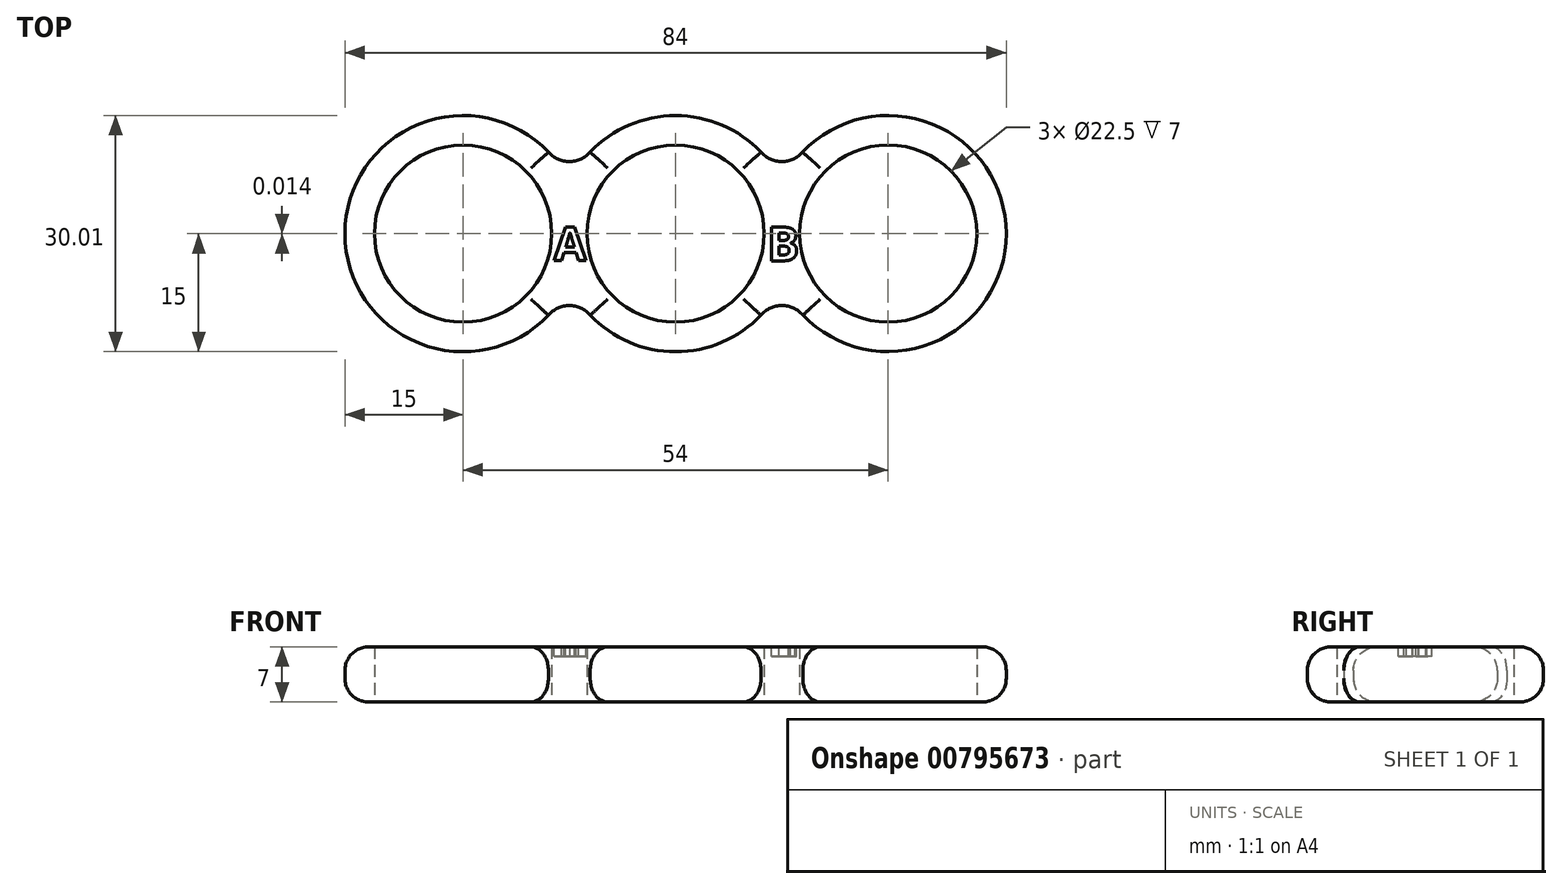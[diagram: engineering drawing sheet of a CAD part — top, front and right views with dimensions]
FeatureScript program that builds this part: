
annotation { "Feature Type Name" : "Feature", "Feature Type Description" : "" }
export const myFeature = defineFeature(function(context is Context, id is Id, definition is map)
    precondition{}
    {
        {
            var Q0;
            Q0=qCreatedBy(makeId("Top.planeOp"),FACE);
            var sketch = newSketch(context, id + "F0", { "sketchPlane" : qUnion([Q0])});
            skCircle(sketch, "E0", {"center": v(0, 0) * mm, "radius": 11.25 * mm});
            skCircle(sketch, "E1", {"center": v(0, 0) * mm, "radius": 4 * mm});
            skCircle(sketch, "E2", {"center": v(27, 0.01) * mm, "radius": 11.25 * mm});
            skCircle(sketch, "E3", {"center": v(27, 0.01) * mm, "radius": 4 * mm});
            skCircle(sketch, "E4", {"center": v(-27, 0) * mm, "radius": 4 * mm});
            skCircle(sketch, "E5", {"center": v(-27, 0) * mm, "radius": 11.25 * mm});
            skPoint(sketch, "E6.first.point", {"position": v(-16.16, 10.36) * mm});
            skPoint(sketch, "E6.second.point", {"position": v(-10.84, 10.36) * mm});
            skPoint(sketch, "E7.first.point", {"position": v(10.84, 10.36) * mm});
            skPoint(sketch, "E7.second.point", {"position": v(16.14, 10.36) * mm});
            skLineSegment(sketch, "E8", {"start": v(-16.16, 10.36) * mm, "end": v(-16.16, 10.36) * mm});
            skArc(sketch, "E9", {"start": v(10.84, 10.36) * mm, "mid": v(13.5, 9.15) * mm, "end": v(16.14, 10.36) * mm});
            skLineSegment(sketch, "E10", {"start": v(16.14, 10.36) * mm, "end": v(16.14, 10.36) * mm});
            skArc(sketch, "E11", {"start": v(10.84, 10.36) * mm, "mid": v(0, 15) * mm, "end": v(-10.84, 10.36) * mm});
            skPoint(sketch, "E12.first.point", {"position": v(-16.15, -10.36) * mm});
            skPoint(sketch, "E12.second.point", {"position": v(-10.85, -10.36) * mm});
            skPoint(sketch, "E12.third.point", {"position": v(-13.67, -16.14) * mm});
            skPoint(sketch, "E13.first.point", {"position": v(10.85, -10.35) * mm});
            skPoint(sketch, "E13.second.point", {"position": v(16.16, -10.35) * mm});
            skPoint(sketch, "E13.third.point", {"position": v(14.19, -16.07) * mm});
            skLineSegment(sketch, "E14", {"start": v(-10.85, -10.36) * mm, "end": v(-10.85, -10.36) * mm});
            skArc(sketch, "E15", {"start": v(-10.85, -10.36) * mm, "mid": v(-13.5, -9.14) * mm, "end": v(-16.15, -10.36) * mm});
            skLineSegment(sketch, "E16", {"start": v(-16.15, -10.36) * mm, "end": v(-16.15, -10.36) * mm});
            skArc(sketch, "E17", {"start": v(-13.5, -6.54) * mm, "mid": v(-13.5, -6.55) * mm, "end": v(-13.49, -6.57) * mm});
            skArc(sketch, "E18", {"start": v(-16.16, 10.36) * mm, "mid": v(-13.5, 9.14) * mm, "end": v(-10.84, 10.36) * mm});
            skArc(sketch, "E19", {"start": v(-16.16, 10.36) * mm, "mid": v(-42, 0) * mm, "end": v(-16.15, -10.36) * mm});
            skArc(sketch, "E20", {"start": v(-10.85, -10.36) * mm, "mid": v(0, -15) * mm, "end": v(10.85, -10.35) * mm});
            skLineSegment(sketch, "E21", {"start": v(-13.49, -6.57) * mm, "end": v(-13.49, -6.57) * mm});
            skArc(sketch, "E22", {"start": v(16.16, -10.35) * mm, "mid": v(42, 0.03) * mm, "end": v(16.14, 10.36) * mm});
            skLineSegment(sketch, "E23", {"start": v(13.5, 6.55) * mm, "end": v(13.5, 6.55) * mm});
            skArc(sketch, "E24", {"start": v(16.16, -10.35) * mm, "mid": v(13.5, -9.14) * mm, "end": v(10.85, -10.35) * mm});
            skLineSegment(sketch, "E25", {"start": v(10.85, -10.35) * mm, "end": v(10.85, -10.35) * mm});
            skArc(sketch, "E26", {"start": v(13.51, 6.51) * mm, "mid": v(13.5, 6.53) * mm, "end": v(13.5, 6.55) * mm});
            skSolve(sketch);
        }
        {
            var Q0;
            Q0=makeQuery(id+"F0.imprint","IMPRINT",FACE,{"disambiguationData":[TD([[makeQuery(id+"F0.imprint","IMPRINT",EDGE,{"derivedFrom":sQuery(id+"F0.wireOp",EDGE,"E0")}),-1.0]])]});
            extrude(context, id + "F1", {"entities" : qUnion([Q0]), "depth" : 7 * mm, "offsetDistance" : 25 * mm});
        }
        {
            var Q0;
            Q0=makeQuery(id+"F1.opExtrude","CAP_EDGE",EDGE,{"disambiguationData":[OSD([sQuery(id+"F0.wireOp",EDGE,"E19")])],"isStart":false});
            var Q1;
            Q1=makeQuery(id+"F1.opExtrude","CAP_EDGE",EDGE,{"disambiguationData":[OSD([sQuery(id+"F0.wireOp",EDGE,"E15")])],"isStart":false});
            var Q2;
            Q2=makeQuery(id+"F1.opExtrude","CAP_EDGE",EDGE,{"disambiguationData":[OSD([sQuery(id+"F0.wireOp",EDGE,"E18")])],"isStart":false});
            var Q3;
            Q3=makeQuery(id+"F1.opExtrude","CAP_EDGE",EDGE,{"disambiguationData":[OSD([sQuery(id+"F0.wireOp",EDGE,"E11")])],"isStart":false});
            var Q4;
            Q4=makeQuery(id+"F1.opExtrude","CAP_EDGE",EDGE,{"disambiguationData":[OSD([sQuery(id+"F0.wireOp",EDGE,"E20")])],"isStart":false});
            var Q5;
            Q5=makeQuery(id+"F1.opExtrude","CAP_EDGE",EDGE,{"disambiguationData":[OSD([sQuery(id+"F0.wireOp",EDGE,"E22")])],"isStart":false});
            var Q6;
            Q6=makeQuery(id+"F1.opExtrude","CAP_EDGE",EDGE,{"disambiguationData":[OSD([sQuery(id+"F0.wireOp",EDGE,"E24")])],"isStart":false});
            var Q7;
            Q7=makeQuery(id+"F1.opExtrude","CAP_EDGE",EDGE,{"disambiguationData":[OSD([sQuery(id+"F0.wireOp",EDGE,"E9")])],"isStart":false});
            var Q8;
            Q8=makeQuery(id+"F1.opExtrude","CAP_EDGE",EDGE,{"disambiguationData":[OSD([sQuery(id+"F0.wireOp",EDGE,"E19")])],"isStart":true});
            var Q9;
            Q9=makeQuery(id+"F1.opExtrude","CAP_EDGE",EDGE,{"disambiguationData":[OSD([sQuery(id+"F0.wireOp",EDGE,"E20")])],"isStart":true});
            var Q10;
            Q10=makeQuery(id+"F1.opExtrude","CAP_EDGE",EDGE,{"disambiguationData":[OSD([sQuery(id+"F0.wireOp",EDGE,"E15")])],"isStart":true});
            var Q11;
            Q11=makeQuery(id+"F1.opExtrude","CAP_EDGE",EDGE,{"disambiguationData":[OSD([sQuery(id+"F0.wireOp",EDGE,"E18")])],"isStart":true});
            var Q12;
            Q12=makeQuery(id+"F1.opExtrude","CAP_EDGE",EDGE,{"disambiguationData":[OSD([sQuery(id+"F0.wireOp",EDGE,"E11")])],"isStart":true});
            var Q13;
            Q13=makeQuery(id+"F1.opExtrude","CAP_EDGE",EDGE,{"disambiguationData":[OSD([sQuery(id+"F0.wireOp",EDGE,"E9")])],"isStart":true});
            var Q14;
            Q14=makeQuery(id+"F1.opExtrude","CAP_EDGE",EDGE,{"disambiguationData":[OSD([sQuery(id+"F0.wireOp",EDGE,"E24")])],"isStart":true});
            var Q15;
            Q15=makeQuery(id+"F1.opExtrude","CAP_EDGE",EDGE,{"disambiguationData":[OSD([sQuery(id+"F0.wireOp",EDGE,"E22")])],"isStart":true});
            fillet(context, id + "F2", {"entities" : qUnion([Q0, Q1, Q2, Q3, Q4, Q5, Q6, Q7, Q8, Q9, Q10, Q11, Q12, Q13, Q14, Q15]), "radius" : 3 * mm, "tangentPropagation" : true, "allowEdgeOverflow" : false});
        }
        {
            var Q0;
            Q0=makeQuery(id+"F1.opExtrude","CAP_FACE",FACE,{"disambiguationData":[OSD([sQuery(id+"F0.wireOp",EDGE,"E0"),sQuery(id+"F0.wireOp",EDGE,"E2"),sQuery(id+"F0.wireOp",EDGE,"E5"),sQuery(id+"F0.wireOp",EDGE,"E9"),sQuery(id+"F0.wireOp",EDGE,"E11"),sQuery(id+"F0.wireOp",EDGE,"E15"),sQuery(id+"F0.wireOp",EDGE,"E18"),sQuery(id+"F0.wireOp",EDGE,"E19"),sQuery(id+"F0.wireOp",EDGE,"E20"),sQuery(id+"F0.wireOp",EDGE,"E22"),sQuery(id+"F0.wireOp",EDGE,"E24")])],"isStart":false});
            var sketch = newSketch(context, id + "F3", { "sketchPlane" : qUnion([Q0])});
            skText(sketch, "E27", { "text": "A", "fontName": "OpenSans-Bold.ttf"});
            skText(sketch, "E28", { "text": "B", "fontName": "OpenSans-Bold.ttf"});
            const initialGuessF3  = {"E27": [-0.01546, -0.00343, 1, 0, 0.00427], "E28": [0.01166, -0.00345, 1, 0, 0.00432]};
            skSetInitialGuess(sketch, initialGuessF3);
            skSolve(sketch);
        }
        {
            var Q0;
            Q0 = qSketchRegion(id + "F3", true);
            extrude(context, id + "F4", {"entities" : qUnion([Q0]), "operationType" : NewBodyOperationType.REMOVE, "oppositeDirection" : true, "depth" : 1.2 * mm, "offsetDistance" : 25 * mm});
        }
    });
